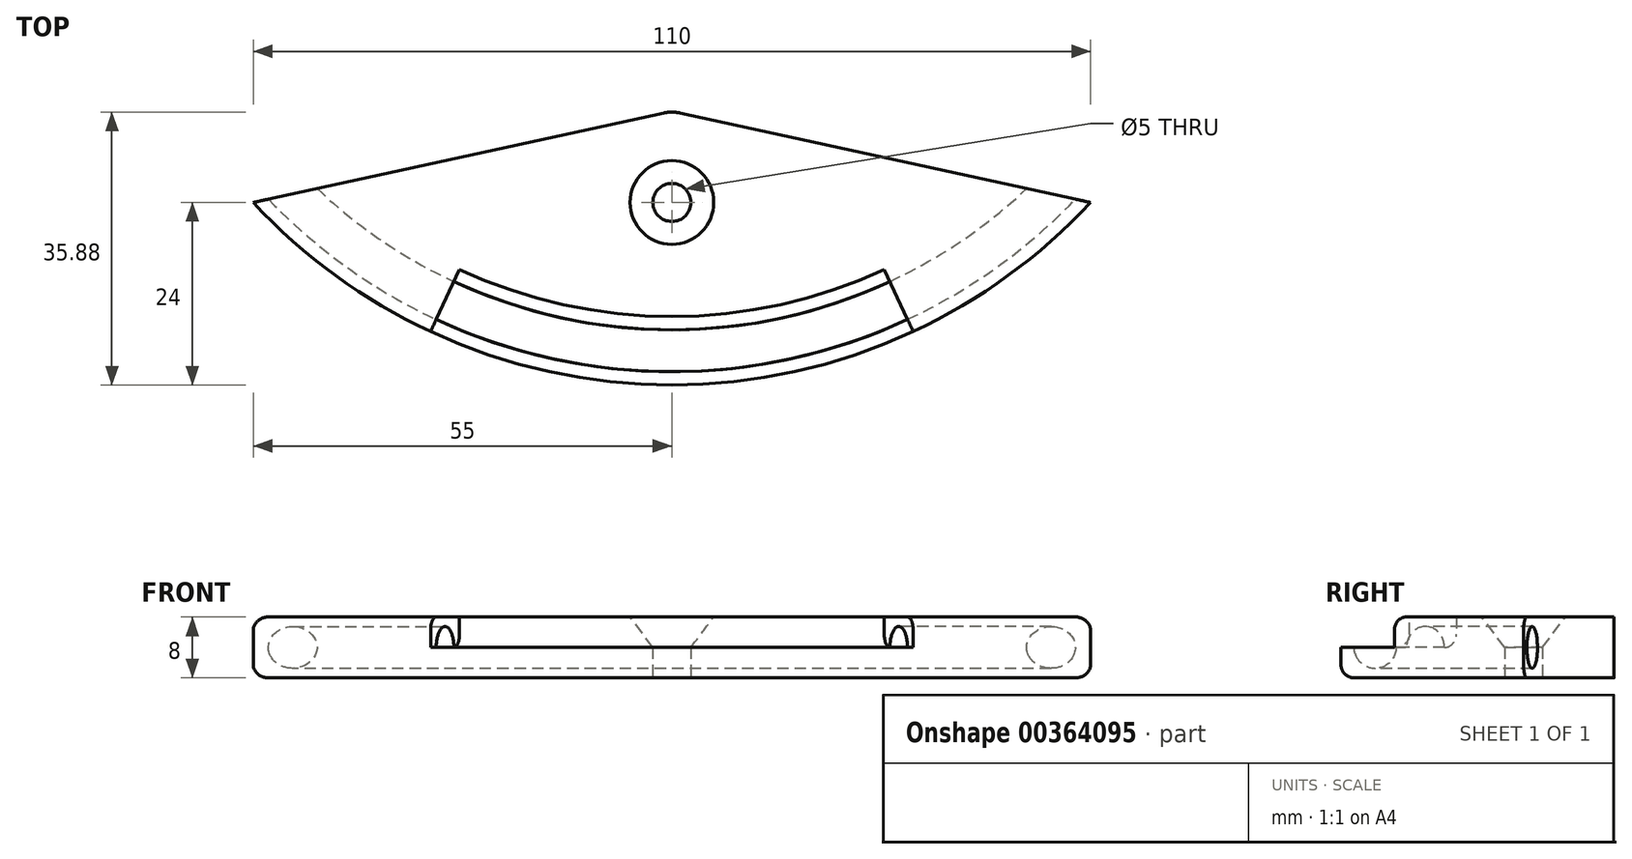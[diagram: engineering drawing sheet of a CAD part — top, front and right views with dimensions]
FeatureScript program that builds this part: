
annotation { "Feature Type Name" : "Feature", "Feature Type Description" : "" }
export const myFeature = defineFeature(function(context is Context, id is Id, definition is map)
    precondition{}
    {
        {
            var Q0;
            Q0=qCreatedBy(makeId("Top.planeOp"),FACE);
            var sketch = newSketch(context, id + "F0", { "sketchPlane" : qUnion([Q0])});
            skCircle(sketch, "E0", {"center": v(0, 0) * mm, "radius": 2.5 * mm});
            skArc(sketch, "E1", {"start": v(-55, 0) * mm, "mid": v(-47.87, -6.74) * mm, "end": v(-39.92, -12.5) * mm});
            skLineSegment(sketch, "E2", {"start": v(-55, 0) * mm, "end": v(0, 12) * mm});
            skLineSegment(sketch, "E3", {"start": v(0, 12) * mm, "end": v(55, 0) * mm});
            skLineSegment(sketch, "E4", {"start": v(0, 12) * mm, "end": v(0, -24) * mm, "construction": true});
            skArc(sketch, "E5", {"start": v(55, 0) * mm, "mid": v(9.8, 125.4) * mm, "end": v(-66.33, 15.97) * mm});
            skArc(sketch, "E6", {"start": v(-39.92, -12.5) * mm, "mid": v(9.8, -23.36) * mm, "end": v(55, 0) * mm});
            skArc(sketch, "E7", {"start": v(-66.33, 15.97) * mm, "mid": v(-61.19, 7.62) * mm, "end": v(-55, 0) * mm});
            skLineSegment(sketch, "E8", {"start": v(-39.92, -12.5) * mm, "end": v(0, 51.02) * mm, "construction": true});
            skLineSegment(sketch, "E9", {"start": v(0, 51.02) * mm, "end": v(-55, 0) * mm, "construction": true});
            skLineSegment(sketch, "E10.MirrorCS", {"start": v(-66.33, 15.97) * mm, "end": v(0, 51.02) * mm, "construction": true});
            skSolve(sketch);
        }
        {
            var Q0;
            Q0=makeQuery(id+"F0.imprint","IMPRINT",FACE,{"disambiguationData":[TD([[makeQuery(id+"F0.imprint","IMPRINT",EDGE,{"derivedFrom":sQuery(id+"F0.wireOp",EDGE,"E0")}),-1.0]])]});
            extrude(context, id + "F1", {"entities" : qUnion([Q0]), "depth" : 8 * mm});
        }
        {
            var Q0;
            Q0=makeQuery(id+"F1.opExtrude","CAP_EDGE",EDGE,{"disambiguationData":[OSD([sQuery(id+"F0.wireOp",EDGE,"E0")])],"isStart":false});
            chamfer(context, id + "F2", {"entities" : qUnion([Q0]), "chamferType" : ChamferType.TWO_OFFSETS, "width1" : 4 * mm, "oppositeDirection" : false, "width2" : 3 * mm, "tangentPropagation" : true});
        }
        {
            var Q0;
            Q0=qCreatedBy(makeId("Right.planeOp"),FACE);
            var sketch = newSketch(context, id + "F3", { "sketchPlane" : qUnion([Q0])});
            skCircle(sketch, "E11", {"center": v(-19.5, 4) * mm, "radius": 2.75 * mm});
            skLineSegment(sketch, "E12.0.0", {"start": v(0, 0) * mm, "end": v(-24, 0) * mm, "construction": true});
            skLineSegment(sketch, "E12.0.1", {"start": v(0, 0) * mm, "end": v(0, 8) * mm, "construction": true});
            skLineSegment(sketch, "E12.0.2", {"start": v(0, 8) * mm, "end": v(-24, 8) * mm, "construction": true});
            skLineSegment(sketch, "E12.0.3", {"start": v(0, 8) * mm, "end": v(0, 0) * mm, "construction": true});
            skLineSegment(sketch, "E13", {"start": v(-24, 8) * mm, "end": v(-24, 0) * mm, "construction": true});
            skLineSegment(sketch, "E14", {"start": v(-19.5, 4) * mm, "end": v(-24, 4) * mm, "construction": true});
            skLineSegment(sketch, "E15.bottom", {"start": v(-24, 8) * mm, "end": v(-15, 8) * mm});
            skLineSegment(sketch, "E15.top", {"start": v(-24, 4) * mm, "end": v(-15, 4) * mm});
            skLineSegment(sketch, "E15.left", {"start": v(-24, 8) * mm, "end": v(-24, 4) * mm});
            skLineSegment(sketch, "E15.right", {"start": v(-15, 8) * mm, "end": v(-15, 4) * mm});
            skPoint(sketch, "E16.0", {"position": v(51.02, 0) * mm});
            skLineSegment(sketch, "E17", {"start": v(51.02, 0) * mm, "end": v(51.02, 8) * mm, "construction": true});
            skSolve(sketch);
        }
        {
            var Q0;
            Q0=makeQuery(id+"F3.imprint","IMPRINT",FACE,{"disambiguationData":[TD([[makeQuery(id+"F3.imprint","IMPRINT",EDGE,{"derivedFrom":sQuery(id+"F3.wireOp",EDGE,"E11")}),1.0]])]});
            var Q1;
            Q1=sQuery(id+"F0.wireOp",EDGE,"E5");
            var Q2;
            Q2=sQuery(id+"F0.wireOp",EDGE,"E1");
            var Q3;
            Q3=sQuery(id+"F0.wireOp",EDGE,"E7");
            var Q4;
            Q4=sQuery(id+"F0.wireOp",EDGE,"E6");
            sweep(context, id + "F4", {"operationType" : NewBodyOperationType.REMOVE, "profiles" : qUnion([Q0]), "path" : qUnion([Q1, Q2, Q3, Q4])});
        }
        {
            var Q0;
            Q0=makeQuery(id+"F3.imprint","IMPRINT",FACE,{"disambiguationData":[TD([[makeQuery(id+"F3.imprint","IMPRINT",EDGE,{"derivedFrom":sQuery(id+"F3.wireOp",EDGE,"E15.bottom")}),-1.0]])]});
            var Q1;
            Q1=sQuery(id+"F3.wireOp",EDGE,"E17");
            revolve(context, id + "F5", {"operationType" : NewBodyOperationType.REMOVE, "entities" : qUnion([Q0]), "axis" : qUnion([Q1]), "revolveType" : RevolveType.SYMMETRIC, "oppositeDirection" : true, "angle" : 50 * degree});
        }
        {
            var Q0;
            Q0=makeQuery(id+"F1.opExtrude","SWEPT_EDGE",EDGE,{"disambiguationData":[OSD([sQuery(id+"F0.wireOp",EDGE,"E2"),sQuery(id+"F0.wireOp",EDGE,"E3")])]});
            fillet(context, id + "F6", {"entities" : qUnion([Q0]), "radius" : 5 * mm, "tangentPropagation" : true, "allowEdgeOverflow" : false});
        }
        {
            var Q0;
            Q0=makeQuery(id+"F1.opExtrude","CAP_EDGE",EDGE,{"disambiguationData":[OSD([sQuery(id+"F0.wireOp",EDGE,"E1")])],"isStart":true});
            var Q1;
            Q1=makeQuery(id+"F1.opExtrude","CAP_EDGE",EDGE,{"disambiguationData":[OSD([sQuery(id+"F0.wireOp",EDGE,"E1")])],"isStart":false});
            var Q2;
            Q2=makeQuery(id+"F5.boolean.opBoolean","COPY",EDGE,{"derivedFrom":makeQuery(id+"F5.opRevolve","SWEPT_EDGE",EDGE,{"disambiguationData":[OSD([sQuery(id+"F3.wireOp",EDGE,"E15.bottom"),sQuery(id+"F3.wireOp",EDGE,"E15.right")])]})});
            var Q3;
            Q3=makeQuery(id+"F5.boolean.opBoolean","COPY",EDGE,{"derivedFrom":makeQuery(id+"F5.opRevolve","SWEPT_EDGE",EDGE,{"disambiguationData":[OSD([sQuery(id+"F3.wireOp",EDGE,"E15.top"),sQuery(id+"F3.wireOp",EDGE,"E15.right")])]})});
            var Q4;
            Q4=makeQuery(id+"F5.boolean.opBoolean","COPY",EDGE,{"derivedFrom":makeQuery(id+"F5.opRevolve","CAP_EDGE",EDGE,{"disambiguationData":[OSD([sQuery(id+"F3.wireOp",EDGE,"E15.bottom")])],"isStart":false})});
            var Q5;
            Q5=makeQuery(id+"F5.boolean.opBoolean","COPY",EDGE,{"derivedFrom":makeQuery(id+"F5.opRevolve","CAP_EDGE",EDGE,{"disambiguationData":[OSD([sQuery(id+"F3.wireOp",EDGE,"E15.bottom")])],"isStart":true})});
            var Q6;
            Q6=makeQuery(id+"F5.boolean.opBoolean","COPY",EDGE,{"derivedFrom":makeQuery(id+"F5.opRevolve","CAP_EDGE",EDGE,{"disambiguationData":[OSD([sQuery(id+"F3.wireOp",EDGE,"E15.left")])],"isStart":true})});
            var Q7;
            Q7=makeQuery(id+"F5.boolean.opBoolean","COPY",EDGE,{"derivedFrom":makeQuery(id+"F5.opRevolve","CAP_EDGE",EDGE,{"disambiguationData":[OSD([sQuery(id+"F3.wireOp",EDGE,"E15.left")])],"isStart":false})});
            fillet(context, id + "F7", {"entities" : qUnion([Q0, Q1, Q2, Q3, Q4, Q5, Q6, Q7]), "radius" : 1.75 * mm, "tangentPropagation" : true, "allowEdgeOverflow" : false});
        }
    });
